# Revit family: SEGA
name_source: partatom
category: Lighting Fixtures
units: mm (PartAtom-declared; Revit-internal decimal feet)

## family parameters
Always vertical = Yes
Cut with Voids When Loaded = No
Light Source = Yes
Maintain Annotation Orientation = No
OmniClass Number = 23.80.70.00
OmniClass Title = Lighting
Part Type = Normal
Room Calculation Point = No
Round Connector Dimension = Use Diameter
Shared = No
Work Plane-Based = No

## types (2) — shared parameters
CRI = 80
Color Filter = 16777215
Default Elevation = 0' - 0"
Dimming Lamp Color Temperature Shift = <None>
IK Rating = 08
IP Rating = 66
Input Voltage = 120-277V
Lamp = LED
Load Classification = Lighting
Manufacturer = Above All Lighting
Power Factor = 0.9
Tilt Angle = 90.00°
URL = https://www.abovealllighting.com

## per-type parameters (varying)
| type | L | Model | Photometric Web File | Wattage Comments |
| SEGA-24W-2ft-RGBW3000K-60°-without bracket/driver | 2' - 0" | SEGA-2421-RGBW30-DMX-60 | SEGA-24W-RGBW3000K-60D.IES | 24W |
| SEGA-36W-3ft-3000K-30°-without bracket/driver | 3' - 0" | SEGA-3631-3080-30 | SEGA-36W-3000K-30D-0-10V with grille.IES | 36W |

## geometry (parser evidence)
native form markers: Sweep x2
no freeform markers — native parametric forms only
